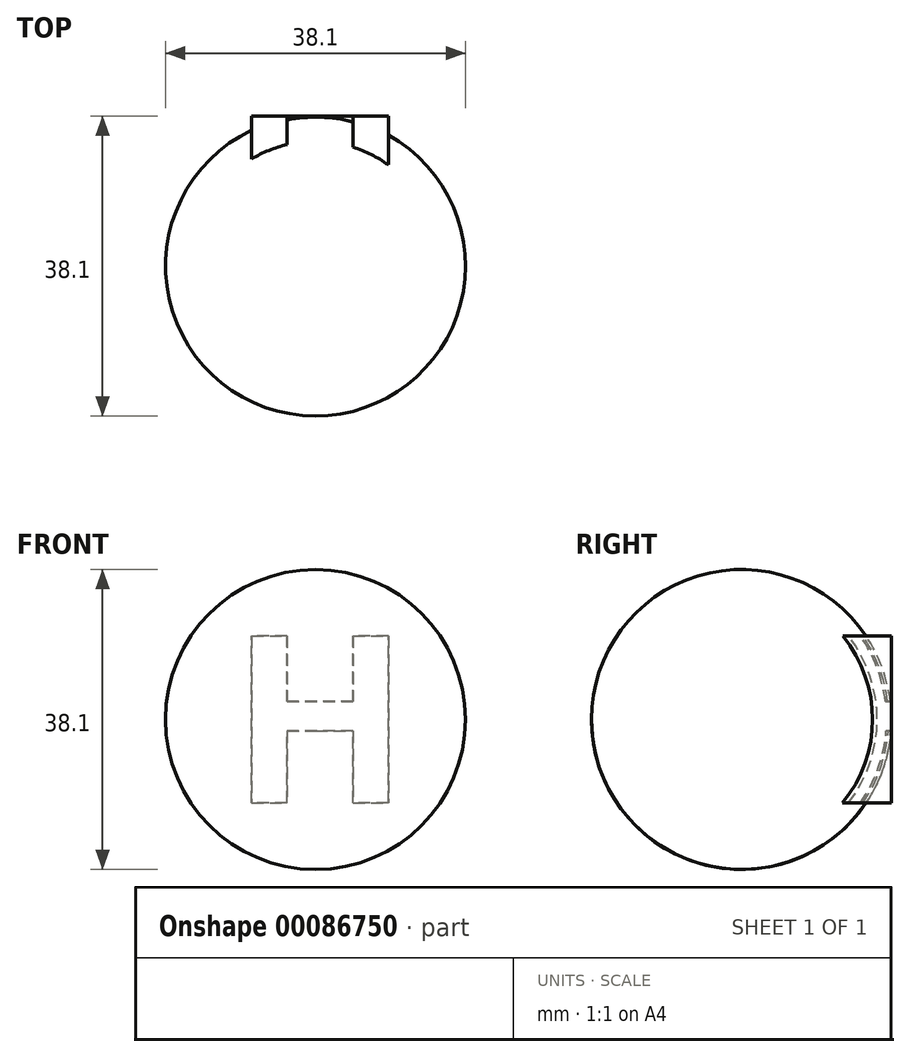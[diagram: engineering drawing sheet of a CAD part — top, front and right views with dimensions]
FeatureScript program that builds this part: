
annotation { "Feature Type Name" : "Feature", "Feature Type Description" : "" }
export const myFeature = defineFeature(function(context is Context, id is Id, definition is map)
    precondition{}
    {
        {
            var Q0;
            Q0=qCreatedBy(makeId("Front.planeOp"),FACE);
            var sketch = newSketch(context, id + "F0", { "sketchPlane" : qUnion([Q0])});
            skCircle(sketch, "E0", {"center": v(-17.11, 21.26) * mm, "radius": 19.05 * mm});
            skSolve(sketch);
        }
        {
            var Q0;
            Q0 = qSketchRegion(id + "F0", true);
            extrude(context, id + "F1", {"entities" : qUnion([Q0]), "depth" : 38.1 * mm});
        }
        {
            var Q0;
            Q0=makeQuery(id+"F1.opExtrude","CAP_EDGE",EDGE,{"disambiguationData":[OSD([sQuery(id+"F0.wireOp",EDGE,"E0")])],"isStart":true});
            var Q1;
            Q1=makeQuery(id+"F1.opExtrude","CAP_EDGE",EDGE,{"disambiguationData":[OSD([sQuery(id+"F0.wireOp",EDGE,"E0")])],"isStart":false});
            fillet(context, id + "F2", {"entities" : qUnion([Q0, Q1]), "radius" : 19.05 * mm, "tangentPropagation" : true, "allowEdgeOverflow" : false});
        }
        {
            var Q0;
            Q0=qCreatedBy(makeId("Front.planeOp"),FACE);
            var sketch = newSketch(context, id + "F3", { "sketchPlane" : qUnion([Q0])});
            skText(sketch, "E1", { "text": "H", "fontName": "OpenSans-Bold.ttf"});
            const initialGuessF3  = {"E1": [-0.02788, 0.01067, 1, 0, 0.02135]};
            skSetInitialGuess(sketch, initialGuessF3);
            skSolve(sketch);
        }
        {
            var Q0;
            Q0=makeQuery(id+"F3.imprint","IMPRINT",FACE,{"disambiguationData":[TD([[makeQuery(id+"F3.imprint","IMPRINT",EDGE,{"derivedFrom":sQuery(id+"F3.wireOp",EDGE,"E1.sketch_text.stroke-0")}),-1.0]])]});
            extrude(context, id + "F4", {"entities" : qUnion([Q0]), "operationType" : NewBodyOperationType.ADD, "depth" : 25.4 * mm});
        }
    });
